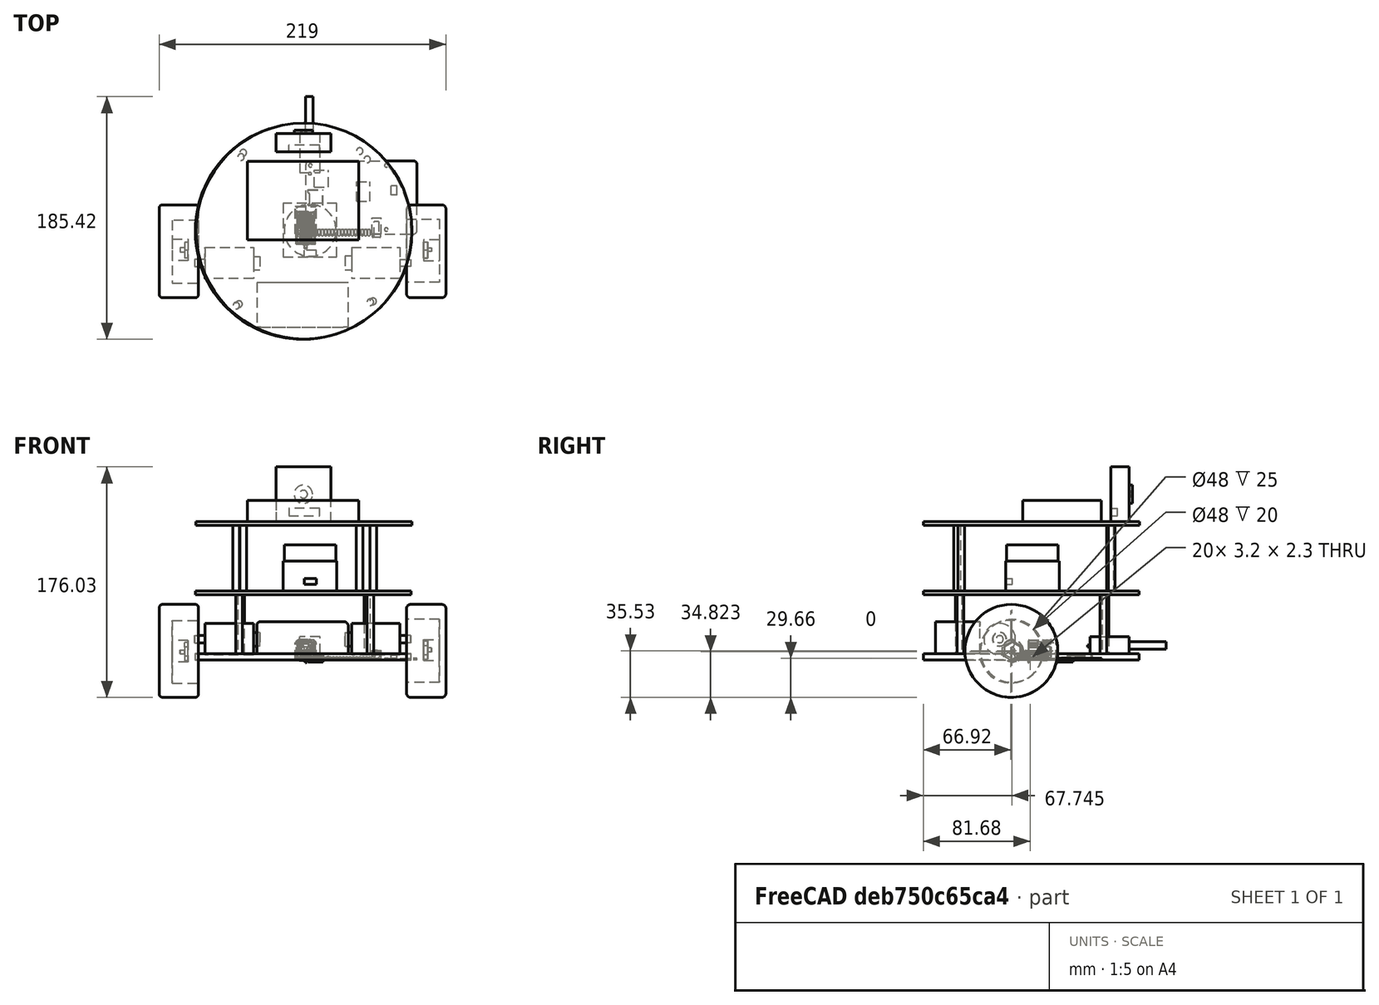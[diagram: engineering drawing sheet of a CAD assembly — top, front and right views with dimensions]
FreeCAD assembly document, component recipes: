
FREECAD ASSEMBLY — COMPONENT RECIPES ("futbot")

This assembly document has 9 components, labeled P0..P8 below (a component is one placed body or linked part). 8 of them carry a construction recipe — the FreeCAD feature program that regenerates the part from scratch, quoted from this document or its linked companion documents; the rest are supplied as boundary geometry only. No exploded tour is included for this assembly.
COMPONENT P0 — recipe-attached ("Cuerpo", modeled in this document).
Construction recipe (the document's own serialized feature program — sketch geometry with constraints, then the solid features built on it; lengths are millimeters unless a unit is written):

FEATURE [Sketcher::SketchObject] Sketch
  ArcFitTolerance = 1e-06
  AttachmentSupport = -> [XY_Plane]
  FullyConstrained = false
  MakeInternals = false
  MapMode = 5
  sketch-geometry (1):
    g0: Circle CenterX=-2.08618 CenterY=2.08626 CenterZ=0 NormalX=0 NormalY=0 NormalZ=1 AngleXU=0 Radius=82.5
  constraints (1):
    c: Diameter(g0) = 165
FEATURE [PartDesign::Pad] Pad
  Direction = (0,0,1)
  Length = 5
  Length2 = 10
  Profile = -> Sketch
  ReferenceAxis = -> Sketch [N_Axis]
  Refine = true
  Suppressed = false
  Type = 0
FEATURE [Sketcher::SketchObject] Sketch002
  ArcFitTolerance = 1e-06
  FullyConstrained = false
  MakeInternals = false
  MapMode = 5
  Placement = pos=(0,0,5) rot=(0,0,1;0rad)
  sketch-geometry (4):
    g0: LineSegment StartX=-37.4321 StartY=-37.1502 StartZ=0 EndX=-37.4321 EndY=-71.1502 EndZ=0
    g1: LineSegment StartX=-37.4321 StartY=-71.1502 StartZ=0 EndX=32.5679 EndY=-71.1502 EndZ=0
    g2: LineSegment StartX=32.5679 StartY=-71.1502 StartZ=0 EndX=32.5679 EndY=-37.1502 EndZ=0
    g3: LineSegment StartX=32.5679 StartY=-37.1502 StartZ=0 EndX=-37.4321 EndY=-37.1502 EndZ=0
  constraints (10):
    c: Coincident(g0,g1)
    c: Coincident(g1,g2)
    c: Coincident(g2,g3)
    c: Coincident(g3,g0)
    c: Vertical(g0)
    c: Vertical(g2)
    c: Horizontal(g1)
    c: Horizontal(g3)
    c: DistanceX(g3,g3) = 70
    c: DistanceY(g2,g2) = 34
FEATURE [PartDesign::Pad] Pad002
  BaseFeature = -> Pad
  Direction = (0,0,1)
  Length = 24.5
  Length2 = 10
  Profile = -> Sketch002
  ReferenceAxis = -> Sketch002 [N_Axis]
  Refine = true
  Suppressed = false
  Type = 0
FEATURE [Sketcher::SketchObject] Sketch003
  ArcFitTolerance = 1e-06
  AttachmentSupport = -> [Pad002]
  FullyConstrained = false
  MakeInternals = false
  MapMode = 5
  Placement = pos=(0,0,5) rot=(0,0,1;0rad)
  sketch-geometry (4):
    g0: Circle CenterX=-49.5124 CenterY=58.8774 CenterZ=0 NormalX=0 NormalY=0 NormalZ=1 AngleXU=0 Radius=2.5
    g1: Circle CenterX=46.9377 CenterY=57.0802 CenterZ=0 NormalX=0 NormalY=0 NormalZ=1 AngleXU=0 Radius=2.5
    g2: Circle CenterX=-51.0101 CenterY=-53.4481 CenterZ=0 NormalX=0 NormalY=0 NormalZ=1 AngleXU=0 Radius=2.5
    g3: Circle CenterX=49.334 CenterY=-51.9504 CenterZ=0 NormalX=0 NormalY=0 NormalZ=1 AngleXU=0 Radius=2.5
  constraints (4):
    c: Diameter(g0) = 5
    c: Diameter(g1) = 5
    c: Diameter(g2) = 5
    c: Diameter(g3) = 5
FEATURE [PartDesign::Pad] Pad003
  BaseFeature = -> Pad002
  Direction = (0,0,1)
  Length = 45
  Length2 = 10
  Profile = -> Sketch003
  ReferenceAxis = -> Sketch003 [N_Axis]
  Refine = true
  Suppressed = false
  Type = 0
FEATURE [PartDesign::Fillet] Fillet
  Base = -> Pad003 [Edge21]
  BaseFeature = -> Pad003
  Radius = 4
  Refine = true
  SupportTransform = false
  Suppressed = false
  UseAllEdges = false
FEATURE [PartDesign::Fillet] Fillet001
  Base = -> Fillet [Edge19]
  BaseFeature = -> Fillet
  Radius = 3
  Refine = true
  SupportTransform = false
  Suppressed = false
  UseAllEdges = false
FEATURE [PartDesign::Plane] DatumPlane
  AttachmentSupport = -> [Fillet001]
  Length = 198.362
  MapMode = 5
  Placement = pos=(0,0,50) rot=(0,0,1;0rad)
  ResizeMode = 0
  Width = 198.078
FEATURE [Sketcher::SketchObject] Sketch008
  ArcFitTolerance = 1e-06
  AttachmentSupport = -> [DatumPlane]
  FullyConstrained = false
  MakeInternals = false
  MapMode = 5
  Placement = pos=(0,0,50) rot=(0,0,1;0rad)
  sketch-geometry (1):
    g0: Circle CenterX=-1.91446 CenterY=2.09682 CenterZ=0 NormalX=0 NormalY=0 NormalZ=1 AngleXU=0 Radius=82.5
  constraints (1):
    c: Diameter(g0) = 165
FEATURE [PartDesign::Pad] Pad004
  BaseFeature = -> Fillet001
  Direction = (0,0,1)
  Length = 3
  Length2 = 10
  Profile = -> Sketch008
  ReferenceAxis = -> Sketch008 [N_Axis]
  Refine = true
  Suppressed = false
  Type = 0
FEATURE [Sketcher::SketchObject] Sketch024
  ArcFitTolerance = 1e-06
  FullyConstrained = false
  MakeInternals = false
  MapMode = 5
  Placement = pos=(0,79.2958,0) rot=(0,0.707107,0.707107;3.14159rad)
  sketch-geometry (4):
    g0: LineSegment StartX=-7.16249 StartY=80.5088 StartZ=0 EndX=-7.16249 EndY=65.5088 EndZ=0
    g1: LineSegment StartX=-7.16249 StartY=65.5088 StartZ=0 EndX=7.83751 EndY=65.5088 EndZ=0
    g2: LineSegment StartX=7.83751 StartY=65.5088 StartZ=0 EndX=7.83751 EndY=80.5088 EndZ=0
    g3: LineSegment StartX=7.83751 StartY=80.5088 StartZ=0 EndX=-7.16249 EndY=80.5088 EndZ=0
  constraints (10):
    c: Coincident(g0,g1)
    c: Coincident(g1,g2)
    c: Coincident(g2,g3)
    c: Coincident(g3,g0)
    c: Vertical(g0)
    c: Vertical(g2)
    c: Horizontal(g1)
    c: Horizontal(g3)
    c: DistanceX(g3,g3) = 15
    c: DistanceY(g2,g2) = 15
FEATURE [PartDesign::Pad] Pad006
  BaseFeature = -> Pad004
  Direction = (1e-16,1,-2e-16)
  Length = 10
  Length2 = 10
  Profile = -> Sketch024
  ReferenceAxis = -> Sketch024 [N_Axis]
  Refine = true
  Suppressed = false
  Type = 0
FEATURE [Sketcher::SketchObject] Sketch026
  ArcFitTolerance = 1e-06
  FullyConstrained = false
  MakeInternals = false
  MapMode = 5
  Placement = pos=(0,0,53) rot=(0,0,1;0rad)
  sketch-geometry (4):
    g0: Circle CenterX=-47.8055 CenterY=62.1638 CenterZ=0 NormalX=0 NormalY=0 NormalZ=1 AngleXU=0 Radius=2.5
    g1: Circle CenterX=41.1821 CenterY=63.4293 CenterZ=0 NormalX=0 NormalY=0 NormalZ=1 AngleXU=0 Radius=2.5
    g2: Circle CenterX=-53.1273 CenterY=-54.6618 CenterZ=0 NormalX=0 NormalY=0 NormalZ=1 AngleXU=0 Radius=2.5
    g3: Circle CenterX=51.4464 CenterY=-51.3399 CenterZ=0 NormalX=0 NormalY=0 NormalZ=1 AngleXU=0 Radius=2.5
  constraints (4):
    c: Diameter(g0) = 5
    c: Diameter(g1) = 5
    c: Diameter(g2) = 5
    c: Diameter(g3) = 5
FEATURE [PartDesign::Pad] Pad008
  BaseFeature = -> Pad006
  Direction = (0,0,1)
  Length = 50
  Length2 = 10
  Profile = -> Sketch026
  ReferenceAxis = -> Sketch026 [N_Axis]
  Refine = true
  Suppressed = false
  Type = 0
FEATURE [PartDesign::Plane] DatumPlane001
  AttachmentSupport = -> [Pad008]
  Length = 198.362
  MapMode = 5
  Placement = pos=(0,0,103) rot=(0,0,1;0rad)
  ResizeMode = 0
  Width = 198.078
FEATURE [Sketcher::SketchObject] Sketch027
  ArcFitTolerance = 1e-06
  AttachmentSupport = -> [DatumPlane001]
  FullyConstrained = false
  MakeInternals = false
  MapMode = 5
  Placement = pos=(0,0,103) rot=(0,0,1;0rad)
  sketch-geometry (1):
    g0: Circle CenterX=-1.38772 CenterY=2.31443 CenterZ=0 NormalX=0 NormalY=0 NormalZ=1 AngleXU=0 Radius=82.5
  constraints (1):
    c: Diameter(g0) = 165
FEATURE [PartDesign::Pad] Pad009
  BaseFeature = -> Pad008
  Direction = (0,0,1)
  Length = 3
  Length2 = 10
  Profile = -> Sketch027
  ReferenceAxis = -> Sketch027 [N_Axis]
  Refine = true
  Suppressed = false
  Type = 0
FEATURE [Sketcher::SketchObject] Sketch051
  ArcFitTolerance = 1e-06
  AttachmentSupport = -> [Pad009]
  FullyConstrained = false
  MakeInternals = false
  MapMode = 5
  Placement = pos=(0,0,106) rot=(0,0,1;0rad)
  sketch-geometry (4):
    g0: LineSegment StartX=-44.6333 StartY=55.601 StartZ=0 EndX=-44.6333 EndY=-4.39901 EndZ=0
    g1: LineSegment StartX=-44.6333 StartY=-4.39901 StartZ=0 EndX=40.3667 EndY=-4.39901 EndZ=0
    g2: LineSegment StartX=40.3667 StartY=-4.39901 StartZ=0 EndX=40.3667 EndY=55.601 EndZ=0
    g3: LineSegment StartX=40.3667 StartY=55.601 StartZ=0 EndX=-44.6333 EndY=55.601 EndZ=0
  constraints (10):
    c: Coincident(g0,g1)
    c: Coincident(g1,g2)
    c: Coincident(g2,g3)
    c: Coincident(g3,g0)
    c: Vertical(g0)
    c: Vertical(g2)
    c: Horizontal(g1)
    c: Horizontal(g3)
    c: DistanceX(g3,g3) = 85
    c: DistanceY(g0,g0) = 60
FEATURE [PartDesign::Pad] Pad025
  BaseFeature = -> Pad009
  Direction = (0,0,1)
  Length = 16
  Length2 = 10
  Profile = -> Sketch051
  ReferenceAxis = -> Sketch051 [N_Axis]
  Refine = true
  Suppressed = false
  Type = 0
FEATURE [PartDesign::Body] Body  label="Cuerpo"
  AllowCompound = false
  Group = -> [Sketch,Pad,Sketch002,Pad002,Sketch003,Pad003,Fillet,Fillet001,DatumPlane,Sketch008,Pad004,Sketch024,Pad006,Sketch026,Pad008,DatumPlane001,Sketch027,Pad009,Sketch051,Pad025]
  Origin = -> Origin
  Tip = -> Pad025
COMPONENT P1 — recipe-attached ("Body008", modeled in this document).
Construction recipe (the document's own serialized feature program — sketch geometry with constraints, then the solid features built on it; lengths are millimeters unless a unit is written):

FEATURE [Sketcher::SketchObject] Sketch030
  ArcFitTolerance = 1e-06
  AttachmentSupport = -> [YZ_Plane021]
  FullyConstrained = false
  MakeInternals = false
  MapMode = 5
  Placement = pos=(0,0,0) rot=(0.57735,0.57735,0.57735;2.0944rad)
  sketch-geometry (1):
    g0: Circle CenterX=-2.0864 CenterY=2.08625 CenterZ=0 NormalX=0 NormalY=0 NormalZ=1 AngleXU=0 Radius=35.5
  constraints (1):
    c: Diameter(g0) = 71
FEATURE [PartDesign::Pad] Pad012
  Direction = (1,0,0)
  Length = 30
  Length2 = 10
  Placement = pos=(0,0,0) rot=(1,1,1;2.0944rad)
  Profile = -> Sketch030
  ReferenceAxis = -> Sketch030 [N_Axis]
  Refine = true
  Suppressed = false
  Type = 0
FEATURE [Sketcher::SketchObject] Sketch031
  ArcFitTolerance = 1e-06
  AttachmentSupport = -> [Pad012]
  FullyConstrained = false
  MakeInternals = false
  MapMode = 5
  Placement = pos=(0,0,0) rot=(0.57735,0.57735,-0.57735;4.18879rad)
  sketch-geometry (1):
    g0: Circle CenterX=-1.66476 CenterY=-2.11974 CenterZ=0 NormalX=0 NormalY=0 NormalZ=1 AngleXU=0 Radius=24
  constraints (1):
    c: Diameter(g0) = 48
FEATURE [PartDesign::Pocket] Pocket
  BaseFeature = -> Pad012
  Direction = (1,0,0)
  Length = 25
  Length2 = 5
  Placement = pos=(0,0,0) rot=(1,1,1;2.0944rad)
  Profile = -> Sketch031
  ReferenceAxis = -> Sketch031 [N_Axis]
  Refine = true
  Suppressed = false
  Type = 0
FEATURE [Sketcher::SketchObject] Sketch032
  ArcFitTolerance = 1e-06
  AttachmentSupport = -> [Pocket]
  FullyConstrained = false
  MakeInternals = false
  MapMode = 5
  Placement = pos=(25,0,0) rot=(0.57735,0.57735,-0.57735;4.18879rad)
  sketch-geometry (1):
    g0: Circle CenterX=-1.35082 CenterY=-2.73267 CenterZ=0 NormalX=0 NormalY=0 NormalZ=1 AngleXU=0 Radius=8
  constraints (1):
    c: Diameter(g0) = 16
FEATURE [PartDesign::Pad] Pad013
  BaseFeature = -> Pocket
  Direction = (-1,0,0)
  Length = 12
  Length2 = 10
  Placement = pos=(0,0,0) rot=(1,1,1;2.0944rad)
  Profile = -> Sketch032
  ReferenceAxis = -> Sketch032 [N_Axis]
  Refine = true
  Suppressed = false
  Type = 0
FEATURE [Sketcher::SketchObject] Sketch033
  ArcFitTolerance = 1e-06
  AttachmentSupport = -> [Pad013]
  FullyConstrained = false
  MakeInternals = false
  MapMode = 5
  Placement = pos=(13,0,0) rot=(0.57735,0.57735,-0.57735;4.18879rad)
  sketch-geometry (7):
    g0: LineSegment StartX=-1.11187 StartY=4.24801 StartZ=0 EndX=-7.22276 EndY=0.700721 EndZ=0
    g1: LineSegment StartX=-7.22276 StartY=0.700721 StartZ=0 EndX=-7.20616 EndY=-6.36511 EndZ=0
    g2: LineSegment StartX=-7.20616 StartY=-6.36511 StartZ=0 EndX=-1.07867 EndY=-9.88365 EndZ=0
    g3: LineSegment StartX=-1.07867 StartY=-9.88365 StartZ=0 EndX=5.03222 EndY=-6.33636 EndZ=0
    g4: LineSegment StartX=5.03222 StartY=-6.33636 StartZ=0 EndX=5.01562 EndY=0.729474 EndZ=0
    g5: LineSegment StartX=5.01562 StartY=0.729474 StartZ=0 EndX=-1.11187 EndY=4.24801 EndZ=0
    g6: Circle [constr] CenterX=-1.09527 CenterY=-2.81782 CenterZ=0 NormalX=0 NormalY=0 NormalZ=1 AngleXU=0 Radius=7.06585
  constraints (13):
    c: Coincident(g0,g1)
    c: Coincident(g1,g2)
    c: Coincident(g2,g3)
    c: Coincident(g3,g4)
    c: Coincident(g4,g5)
    c: Coincident(g5,g0)
    c: Equal(g0, g1-g5) x5
    c: PointOnObject(g0,g6)
    c: PointOnObject(g1,g6)
    c: PointOnObject(g2,g6)
    c: PointOnObject(g3,g6)
    c: PointOnObject(g4,g6)
    c: PointOnObject(g5,g6)
FEATURE [PartDesign::Pocket] Pocket001
  BaseFeature = -> Pad013
  Direction = (1,0,0)
  Length = 3
  Length2 = 5
  Placement = pos=(0,0,0) rot=(1,1,1;2.0944rad)
  Profile = -> Sketch033
  ReferenceAxis = -> Sketch033 [N_Axis]
  Refine = true
  Suppressed = false
  Type = 0
FEATURE [Sketcher::SketchObject] Sketch004
  ArcFitTolerance = 1e-06
  AttachmentSupport = -> [Pocket001]
  FullyConstrained = false
  MakeInternals = false
  MapMode = 5
  Placement = pos=(16,0,0) rot=(0.57735,0.57735,-0.57735;4.18879rad)
  sketch-geometry (1):
    g0: Circle CenterX=-0.927213 CenterY=-2.79304 CenterZ=0 NormalX=0 NormalY=0 NormalZ=1 AngleXU=0 Radius=1.5
  constraints (1):
    c: Diameter(g0) = 3
FEATURE [PartDesign::Pocket] Pocket002
  BaseFeature = -> Pocket001
  Direction = (1,0,0)
  Length = 3
  Length2 = 5
  Placement = pos=(0,0,0) rot=(1,1,1;2.0944rad)
  Profile = -> Sketch004
  ReferenceAxis = -> Sketch004 [N_Axis]
  Refine = true
  Suppressed = false
  Type = 0
FEATURE [PartDesign::Fillet] Fillet016  label="Fillet018"
  Base = -> Pocket002 [Edge2]
  BaseFeature = -> Pocket002
  Placement = pos=(0,0,0) rot=(1,1,1;2.0944rad)
  Radius = 3
  Refine = true
  SupportTransform = false
  Suppressed = false
  UseAllEdges = false
FEATURE [PartDesign::Fillet] Fillet017  label="Fillet019"
  Base = -> Fillet016 [Edge3]
  BaseFeature = -> Fillet016
  Placement = pos=(0,0,0) rot=(1,1,1;2.0944rad)
  Radius = 3
  Refine = true
  SupportTransform = false
  Suppressed = false
  UseAllEdges = false
FEATURE [PartDesign::Body] Body001  label="Body008"
  AllowCompound = false
  Group = -> [Sketch030,Pad012,Sketch031,Pocket,Sketch032,Pad013,Sketch033,Pocket001,Sketch004,Pocket002,Fillet016,Fillet017]
  Origin = -> Origin021
  Placement = pos=(77,-11,5) rot=(0,0,1;0rad)
  Tip = -> Fillet017
COMPONENT P2 — recipe-attached ("Body009", modeled in this document).
Construction recipe (the document's own serialized feature program — sketch geometry with constraints, then the solid features built on it; lengths are millimeters unless a unit is written):

FEATURE [Sketcher::SketchObject] Sketch034
  ArcFitTolerance = 1e-06
  AttachmentSupport = -> [YZ_Plane022]
  FullyConstrained = false
  MakeInternals = false
  MapMode = 5
  Placement = pos=(0,0,0) rot=(0.57735,0.57735,0.57735;2.0944rad)
  sketch-geometry (1):
    g0: Circle CenterX=-2.08628 CenterY=2.08615 CenterZ=0 NormalX=0 NormalY=0 NormalZ=1 AngleXU=0 Radius=35.5
  constraints (1):
    c: Diameter(g0) = 71
FEATURE [PartDesign::Pad] Pad014
  Direction = (1,0,0)
  Length = 30
  Length2 = 10
  Placement = pos=(0,0,0) rot=(1,1,1;2.0944rad)
  Profile = -> Sketch034
  ReferenceAxis = -> Sketch034 [N_Axis]
  Refine = true
  Suppressed = false
  Type = 0
FEATURE [Sketcher::SketchObject] Sketch035
  ArcFitTolerance = 1e-06
  AttachmentSupport = -> [Pad014]
  FullyConstrained = false
  MakeInternals = false
  MapMode = 5
  Placement = pos=(30,0,0) rot=(0.57735,0.57735,0.57735;2.0944rad)
  sketch-geometry (1):
    g0: Circle CenterX=-2.49007 CenterY=1.41343 CenterZ=0 NormalX=0 NormalY=0 NormalZ=1 AngleXU=0 Radius=24
  constraints (1):
    c: Diameter(g0) = 48
FEATURE [PartDesign::Fillet] Fillet018  label="Fillet020"
  Base = -> Pad014 [Edge3]
  BaseFeature = -> Pad014
  Placement = pos=(0,0,0) rot=(1,1,1;2.0944rad)
  Radius = 2.5
  Refine = true
  SupportTransform = false
  Suppressed = false
  UseAllEdges = false
FEATURE [PartDesign::Fillet] Fillet019  label="Fillet021"
  Base = -> Fillet018 [Edge3]
  BaseFeature = -> Fillet018
  Placement = pos=(0,0,0) rot=(1,1,1;2.0944rad)
  Radius = 2.5
  Refine = true
  SupportTransform = false
  Suppressed = false
  UseAllEdges = false
FEATURE [PartDesign::Pocket] Pocket003
  BaseFeature = -> Fillet019
  Direction = (-1,0,0)
  Length = 20
  Length2 = 5
  Placement = pos=(0,0,0) rot=(1,1,1;2.0944rad)
  Profile = -> Sketch035
  ReferenceAxis = -> Sketch035 [N_Axis]
  Refine = true
  Suppressed = false
  Type = 0
FEATURE [Sketcher::SketchObject] Sketch036
  ArcFitTolerance = 1e-06
  AttachmentSupport = -> [Pocket003]
  FullyConstrained = false
  MakeInternals = false
  MapMode = 5
  Placement = pos=(10,0,0) rot=(0.57735,0.57735,0.57735;2.0944rad)
  sketch-geometry (1):
    g0: Circle CenterX=-1.10678 CenterY=1.90225 CenterZ=0 NormalX=0 NormalY=0 NormalZ=1 AngleXU=0 Radius=8.25
  constraints (1):
    c: Diameter(g0) = 16.5
FEATURE [PartDesign::Pad] Pad015
  BaseFeature = -> Pocket003
  Direction = (1,0,0)
  Length = 12
  Length2 = 10
  Placement = pos=(0,0,0) rot=(1,1,1;2.0944rad)
  Profile = -> Sketch036
  ReferenceAxis = -> Sketch036 [N_Axis]
  Refine = true
  Suppressed = false
  Type = 0
FEATURE [Sketcher::SketchObject] Sketch037
  ArcFitTolerance = 1e-06
  AttachmentSupport = -> [Pad015]
  FullyConstrained = false
  MakeInternals = false
  MapMode = 5
  Placement = pos=(22,0,0) rot=(0.57735,0.57735,0.57735;2.0944rad)
  sketch-geometry (7):
    g0: LineSegment StartX=4.85295 StartY=4.98885 StartZ=0 EndX=-1.20923 EndY=8.48885 EndZ=0
    g1: LineSegment StartX=-1.20923 StartY=8.48885 StartZ=0 EndX=-7.27141 EndY=4.98885 EndZ=0
    g2: LineSegment StartX=-7.27141 StartY=4.98885 StartZ=0 EndX=-7.27141 EndY=-2.01115 EndZ=0
    g3: LineSegment StartX=-7.27141 StartY=-2.01115 StartZ=0 EndX=-1.20923 EndY=-5.51115 EndZ=0
    g4: LineSegment StartX=-1.20923 StartY=-5.51115 StartZ=0 EndX=4.85295 EndY=-2.01115 EndZ=0
    g5: LineSegment StartX=4.85295 StartY=-2.01115 StartZ=0 EndX=4.85295 EndY=4.98885 EndZ=0
    g6: Circle [constr] CenterX=-1.20923 CenterY=1.48885 CenterZ=0 NormalX=0 NormalY=0 NormalZ=1 AngleXU=0 Radius=7
  constraints (15):
    c: Coincident(g0,g1)
    c: Coincident(g1,g2)
    c: Coincident(g2,g3)
    c: Coincident(g3,g4)
    c: Coincident(g4,g5)
    c: Coincident(g5,g0)
    c: Equal(g0, g1-g5) x5
    c: PointOnObject(g0,g6)
    c: PointOnObject(g1,g6)
    c: PointOnObject(g2,g6)
    c: PointOnObject(g3,g6)
    c: PointOnObject(g4,g6)
    c: PointOnObject(g5,g6)
    c: Distance(g0,g0) = 7
    c: DistanceY(g5,g5) = 7
FEATURE [PartDesign::Pocket] Pocket004
  BaseFeature = -> Pad015
  Direction = (-1,0,0)
  Length = 2.5
  Length2 = 5
  Placement = pos=(0,0,0) rot=(1,1,1;2.0944rad)
  Profile = -> Sketch037
  ReferenceAxis = -> Sketch037 [N_Axis]
  Refine = true
  Suppressed = false
  Type = 0
FEATURE [Sketcher::SketchObject] Sketch038
  ArcFitTolerance = 1e-06
  AttachmentSupport = -> [Pocket004]
  FullyConstrained = false
  MakeInternals = false
  MapMode = 5
  Placement = pos=(19.5,0,0) rot=(0.57735,0.57735,0.57735;2.0944rad)
  sketch-geometry (1):
    g0: Circle CenterX=-1.04009 CenterY=1.34355 CenterZ=0 NormalX=0 NormalY=0 NormalZ=1 AngleXU=0 Radius=1.5
  constraints (1):
    c: Diameter(g0) = 3
FEATURE [PartDesign::Pocket] Pocket005
  BaseFeature = -> Pocket004
  Direction = (-1,0,0)
  Length = 3.5
  Length2 = 5
  Placement = pos=(0,0,0) rot=(1,1,1;2.0944rad)
  Profile = -> Sketch038
  ReferenceAxis = -> Sketch038 [N_Axis]
  Refine = true
  Suppressed = false
  Type = 0
FEATURE [PartDesign::Body] Body002  label="Body009"
  AllowCompound = false
  Group = -> [Sketch034,Pad014,Sketch035,Fillet018,Fillet019,Pocket003,Sketch036,Pad015,Sketch037,Pocket004,Sketch038,Pocket005]
  Origin = -> Origin022
  Placement = pos=(-112,-11,5) rot=(0,0,1;0rad)
  Tip = -> Pocket005
COMPONENT P3 — recipe-attached ("Body010", modeled in this document).
Construction recipe (the document's own serialized feature program — sketch geometry with constraints, then the solid features built on it; lengths are millimeters unless a unit is written):

FEATURE [Sketcher::SketchObject] Sketch039
  ArcFitTolerance = 1e-06
  AttachmentSupport = -> [XY_Plane023]
  FullyConstrained = false
  MakeInternals = false
  MapMode = 5
  sketch-geometry (4):
    g0: LineSegment StartX=-17.3005 StartY=23.5417 StartZ=0 EndX=-17.3005 EndY=-17.4583 EndZ=0
    g1: LineSegment StartX=-17.3005 StartY=-17.4583 StartZ=0 EndX=23.6995 EndY=-17.4583 EndZ=0
    g2: LineSegment StartX=23.6995 StartY=-17.4583 StartZ=0 EndX=23.6995 EndY=23.5417 EndZ=0
    g3: LineSegment StartX=23.6995 StartY=23.5417 StartZ=0 EndX=-17.3005 EndY=23.5417 EndZ=0
  constraints (10):
    c: Coincident(g0,g1)
    c: Coincident(g1,g2)
    c: Coincident(g2,g3)
    c: Coincident(g3,g0)
    c: Vertical(g0)
    c: Vertical(g2)
    c: Horizontal(g1)
    c: Horizontal(g3)
    c: DistanceX(g1,g1) = 41
    c: DistanceY(g0,g0) = 41
FEATURE [PartDesign::Pad] Pad016
  Direction = (0,0,1)
  Length = 22.6
  Length2 = 10
  Profile = -> Sketch039
  ReferenceAxis = -> Sketch039 [N_Axis]
  Refine = true
  Suppressed = false
  Type = 0
FEATURE [Sketcher::SketchObject] Sketch040
  ArcFitTolerance = 1e-06
  AttachmentSupport = -> [Pad016]
  FullyConstrained = false
  MakeInternals = false
  MapMode = 5
  Placement = pos=(0,0,22.6) rot=(0,0,1;0rad)
  sketch-geometry (1):
    g0: Circle CenterX=3.29703 CenterY=2.8924 CenterZ=0 NormalX=0 NormalY=0 NormalZ=1 AngleXU=0 Radius=19.8
  constraints (1):
    c: Diameter(g0) = 39.6
FEATURE [PartDesign::Pad] Pad017
  BaseFeature = -> Pad016
  Direction = (0,0,1)
  Length = 12.6
  Length2 = 10
  Profile = -> Sketch040
  ReferenceAxis = -> Sketch040 [N_Axis]
  Refine = true
  Suppressed = false
  Type = 0
FEATURE [Sketcher::SketchObject] Sketch041
  ArcFitTolerance = 1e-06
  AttachmentSupport = -> [Pad017]
  FullyConstrained = false
  MakeInternals = false
  MapMode = 5
  Placement = pos=(0,-17.4583,0) rot=(1,0,0;1.5708rad)
  sketch-geometry (5):
    g0: LineSegment StartX=-1.04287 StartY=9.49271 StartZ=0 EndX=-1.04287 EndY=4.79271 EndZ=0
    g1: LineSegment StartX=-1.04287 StartY=4.79271 StartZ=0 EndX=7.95713 EndY=4.79271 EndZ=0
    g2: LineSegment StartX=7.95713 StartY=4.79271 StartZ=0 EndX=7.95713 EndY=9.49271 EndZ=0
    g3: LineSegment StartX=7.95713 StartY=9.49271 StartZ=0 EndX=-1.04287 EndY=9.49271 EndZ=0
    g4: GeomPoint [constr] X=3.45713 Y=7.14271 Z=0
  constraints (11):
    c: Coincident(g0,g1)
    c: Coincident(g1,g2)
    c: Coincident(g2,g3)
    c: Coincident(g3,g0)
    c: Vertical(g0)
    c: Vertical(g2)
    c: Horizontal(g1)
    c: Horizontal(g3)
    c: Symmetric(g2,g0,g4)
    c: DistanceX(g3,g3) = 9
    c: DistanceY(g2,g2) = 4.7
FEATURE [PartDesign::Pocket] Pocket006
  BaseFeature = -> Pad017
  Direction = (0,1,-2e-16)
  Length = 5
  Length2 = 5
  Profile = -> Sketch041
  ReferenceAxis = -> Sketch041 [N_Axis]
  Refine = true
  Suppressed = false
  Type = 0
FEATURE [PartDesign::Body] Body003  label="Body010"
  AllowCompound = false
  Group = -> [Sketch039,Pad016,Sketch040,Pad017,Sketch041,Pocket006]
  Origin = -> Origin023
  Placement = pos=(0,0,53) rot=(0,0,1;0rad)
  Tip = -> Pocket006
COMPONENT P4 — recipe-attached ("Body011", modeled in this document).
Construction recipe (the document's own serialized feature program — sketch geometry with constraints, then the solid features built on it; lengths are millimeters unless a unit is written):

FEATURE [Sketcher::SketchObject] Sketch042
  ArcFitTolerance = 1e-06
  AttachmentSupport = -> [YZ_Plane024]
  FullyConstrained = true
  MakeInternals = false
  MapMode = 5
  Placement = pos=(0,0,0) rot=(0.57735,0.57735,0.57735;2.0944rad)
  sketch-geometry (1):
    g0: Circle CenterX=0 CenterY=0 CenterZ=0 NormalX=0 NormalY=0 NormalZ=1 AngleXU=0 Radius=12
  constraints (2):
    c: Coincident(g0,g-1)
    c: Diameter(g0) = 24
FEATURE [PartDesign::Pad] Pad018
  Direction = (1,0,0)
  Length = 37
  Length2 = 10
  Placement = pos=(0,0,0) rot=(1,1,1;2.0944rad)
  Profile = -> Sketch042
  ReferenceAxis = -> Sketch042 [N_Axis]
  Refine = true
  Suppressed = false
  Type = 0
FEATURE [Sketcher::SketchObject] Sketch001
  ArcFitTolerance = 1e-06
  AttachmentSupport = -> [Pad018]
  FullyConstrained = false
  MakeInternals = false
  MapMode = 5
  Placement = pos=(37,0,0) rot=(0.57735,0.57735,0.57735;2.0944rad)
  sketch-geometry (1):
    g0: Circle CenterX=-0.336656 CenterY=0 CenterZ=0 NormalX=0 NormalY=0 NormalZ=1 AngleXU=0 Radius=5.25
  constraints (2):
    c: PointOnObject(g0,g-1)
    c: Diameter(g0) = 10.5
FEATURE [PartDesign::Pad] Pad001
  BaseFeature = -> Pad018
  Direction = (1,0,0)
  Length = 5
  Length2 = 10
  Placement = pos=(0,0,0) rot=(1,1,1;2.0944rad)
  Profile = -> Sketch001
  ReferenceAxis = -> Sketch001 [N_Axis]
  Refine = true
  Suppressed = false
  Type = 0
FEATURE [Sketcher::SketchObject] Sketch043
  ArcFitTolerance = 1e-06
  AttachmentSupport = -> [Pad001]
  FullyConstrained = true
  MakeInternals = false
  MapMode = 5
  Placement = pos=(0,0,0) rot=(0.57735,0.57735,-0.57735;4.18879rad)
  sketch-geometry (1):
    g0: Circle CenterX=0 CenterY=0 CenterZ=0 NormalX=0 NormalY=0 NormalZ=1 AngleXU=0 Radius=2.75
  constraints (2):
    c: Coincident(g0,g-1)
    c: Diameter(g0) = 5.5
FEATURE [PartDesign::Pad] Pad019
  BaseFeature = -> Pad001
  Direction = (-1,0,0)
  Length = 8
  Length2 = 10
  Placement = pos=(0,0,0) rot=(1,1,1;2.0944rad)
  Profile = -> Sketch043
  ReferenceAxis = -> Sketch043 [N_Axis]
  Refine = true
  Suppressed = false
  Type = 0
  UseCustomVector = true
FEATURE [PartDesign::Body] Body004  label="Body011"
  AllowCompound = false
  Group = -> [Sketch042,Pad018,Sketch001,Pad001,Sketch043,Pad019]
  Origin = -> Origin024
  Placement = pos=(-77,-22,16) rot=(0,0,1;0rad)
  Tip = -> Pad019
COMPONENT P5 — recipe-attached ("Body012", modeled in this document).
Construction recipe (the document's own serialized feature program — sketch geometry with constraints, then the solid features built on it; lengths are millimeters unless a unit is written):

FEATURE [Sketcher::SketchObject] Sketch044
  ArcFitTolerance = 1e-06
  AttachmentSupport = -> [YZ_Plane025]
  FullyConstrained = true
  MakeInternals = false
  MapMode = 5
  Placement = pos=(0,0,0) rot=(0.57735,0.57735,0.57735;2.0944rad)
  sketch-geometry (1):
    g0: Circle CenterX=0 CenterY=0 CenterZ=0 NormalX=0 NormalY=0 NormalZ=1 AngleXU=0 Radius=12
  constraints (2):
    c: Coincident(g0,g-1)
    c: Diameter(g0) = 24
FEATURE [PartDesign::Pad] Pad020
  Direction = (1,0,0)
  Length = 37
  Length2 = 10
  Placement = pos=(0,0,0) rot=(1,1,1;2.0944rad)
  Profile = -> Sketch044
  ReferenceAxis = -> Sketch044 [N_Axis]
  Refine = true
  Suppressed = false
  Type = 0
FEATURE [Sketcher::SketchObject] Sketch045
  ArcFitTolerance = 1e-06
  AttachmentSupport = -> [Pad020]
  FullyConstrained = true
  MakeInternals = false
  MapMode = 5
  Placement = pos=(37,0,0) rot=(0.57735,0.57735,0.57735;2.0944rad)
  sketch-geometry (1):
    g0: Circle CenterX=0 CenterY=0 CenterZ=0 NormalX=0 NormalY=0 NormalZ=1 AngleXU=0 Radius=2.75
  constraints (2):
    c: Coincident(g0,g-1)
    c: Diameter(g0) = 5.5
FEATURE [PartDesign::Pad] Pad021
  BaseFeature = -> Pad020
  Direction = (1,0,0)
  Length = 8
  Length2 = 10
  Placement = pos=(0,0,0) rot=(1,1,1;2.0944rad)
  Profile = -> Sketch045
  ReferenceAxis = -> Sketch045 [N_Axis]
  Refine = true
  Suppressed = false
  Type = 0
FEATURE [Sketcher::SketchObject] Sketch046
  ArcFitTolerance = 1e-06
  AttachmentSupport = -> [Pad021]
  FullyConstrained = true
  MakeInternals = false
  MapMode = 5
  Placement = pos=(0,0,0) rot=(0.57735,0.57735,-0.57735;4.18879rad)
  sketch-geometry (1):
    g0: Circle CenterX=0 CenterY=0 CenterZ=0 NormalX=0 NormalY=0 NormalZ=1 AngleXU=0 Radius=5.25
  constraints (2):
    c: Coincident(g0,g-1)
    c: Diameter(g0) = 10.5
FEATURE [PartDesign::Pad] Pad022
  BaseFeature = -> Pad021
  Direction = (-1,0,0)
  Length = 5
  Length2 = 10
  Placement = pos=(0,0,0) rot=(1,1,1;2.0944rad)
  Profile = -> Sketch046
  ReferenceAxis = -> Sketch046 [N_Axis]
  Refine = true
  Suppressed = false
  Type = 0
FEATURE [PartDesign::Body] Body005  label="Body012"
  AllowCompound = false
  Group = -> [Sketch044,Pad020,Sketch045,Pad021,Sketch046,Pad022]
  Origin = -> Origin025
  Placement = pos=(35,-22,16) rot=(0,0,1;0rad)
  Tip = -> Pad022
COMPONENT P6 — recipe-attached ("Body013", modeled in this document).
Construction recipe (the document's own serialized feature program — sketch geometry with constraints, then the solid features built on it; lengths are millimeters unless a unit is written):

FEATURE [Sketcher::SketchObject] Sketch047
  ArcFitTolerance = 1e-06
  AttachmentSupport = -> [XZ_Plane026]
  FullyConstrained = false
  MakeInternals = false
  MapMode = 5
  Placement = pos=(0,0,0) rot=(1,0,0;1.5708rad)
  sketch-geometry (4):
    g0: LineSegment StartX=-12.8525 StartY=11.6213 StartZ=0 EndX=-12.8525 EndY=-30.3787 EndZ=0
    g1: LineSegment StartX=-12.8525 StartY=-30.3787 StartZ=0 EndX=29.1475 EndY=-30.3787 EndZ=0
    g2: LineSegment StartX=29.1475 StartY=-30.3787 StartZ=0 EndX=29.1475 EndY=11.6213 EndZ=0
    g3: LineSegment StartX=29.1475 StartY=11.6213 StartZ=0 EndX=-12.8525 EndY=11.6213 EndZ=0
  constraints (10):
    c: Coincident(g0,g1)
    c: Coincident(g1,g2)
    c: Coincident(g2,g3)
    c: Coincident(g3,g0)
    c: Vertical(g0)
    c: Vertical(g2)
    c: Horizontal(g1)
    c: Horizontal(g3)
    c: DistanceX(g3,g3) = 42
    c: DistanceY(g0,g0) = 42
FEATURE [PartDesign::Pad] Pad023
  Direction = (0,-1,2e-16)
  Length = 14
  Length2 = 10
  Placement = pos=(0,0,0) rot=(1,0,0;1.5708rad)
  Profile = -> Sketch047
  ReferenceAxis = -> Sketch047 [N_Axis]
  Refine = true
  Suppressed = false
  Type = 0
FEATURE [Sketcher::SketchObject] Sketch048
  ArcFitTolerance = 1e-06
  AttachmentSupport = -> [Pad023]
  FullyConstrained = false
  MakeInternals = false
  MapMode = 5
  Placement = pos=(0,-2.1e-15,0) rot=(-1,0,0;1.5708rad)
  sketch-geometry (1):
    g0: Circle CenterX=8.14286 CenterY=9.21914 CenterZ=0 NormalX=0 NormalY=0 NormalZ=1 AngleXU=0 Radius=7
  constraints (1):
    c: Diameter(g0) = 14
FEATURE [PartDesign::Pad] Pad024
  BaseFeature = -> Pad023
  Direction = (0,1,2e-16)
  Length = 2.5
  Length2 = 10
  Placement = pos=(0,0,0) rot=(1,0,0;1.5708rad)
  Profile = -> Sketch048
  ReferenceAxis = -> Sketch048 [N_Axis]
  Refine = true
  Suppressed = false
  Type = 0
FEATURE [Sketcher::SketchObject] Sketch049
  ArcFitTolerance = 1e-06
  AttachmentSupport = -> [Pad024]
  FullyConstrained = false
  MakeInternals = false
  MapMode = 5
  Placement = pos=(0,2.5,0) rot=(-1,0,0;1.5708rad)
  sketch-geometry (1):
    g0: Circle CenterX=8.27745 CenterY=9.21909 CenterZ=0 NormalX=0 NormalY=0 NormalZ=1 AngleXU=0 Radius=5.62223
FEATURE [PartDesign::Hole] Hole
  BaseFeature = -> Pad024
  CustomThreadClearance = 0
  Depth = 0.5
  DepthType = 0
  Diameter = 6
  DrillForDepth = false
  DrillPoint = 1
  DrillPointAngle = 118
  HoleCutCountersinkAngle = 90
  HoleCutCustomValues = false
  HoleCutDepth = 0
  HoleCutDiameter = 6.1
  HoleCutType = 0
  ModelThread = false
  Placement = pos=(0,0,0) rot=(1,0,0;1.5708rad)
  Profile = -> Sketch049
  Refine = true
  Suppressed = false
  Tapered = false
  TaperedAngle = 90
  ThreadClass = 0
  ThreadDepth = 0.5
  ThreadDepthType = 0
  ThreadDirection = 0
  ThreadFit = 0
  ThreadSize = 0
  ThreadType = 0
  Threaded = false
  UseCustomThreadClearance = false
FEATURE [Sketcher::SketchObject] Sketch050
  ArcFitTolerance = 1e-06
  AttachmentSupport = -> [Hole]
  FullyConstrained = false
  MakeInternals = false
  MapMode = 5
  Placement = pos=(0,-14,0) rot=(1,0,0;1.5708rad)
  sketch-geometry (4):
    g0: LineSegment StartX=-3.02818 StartY=-20.0516 StartZ=0 EndX=-3.02818 EndY=-25.5516 EndZ=0
    g1: LineSegment StartX=-3.02818 StartY=-25.5516 StartZ=0 EndX=20.4718 EndY=-25.5516 EndZ=0
    g2: LineSegment StartX=20.4718 StartY=-25.5516 StartZ=0 EndX=20.4718 EndY=-20.0516 EndZ=0
    g3: LineSegment StartX=20.4718 StartY=-20.0516 StartZ=0 EndX=-3.02818 EndY=-20.0516 EndZ=0
  constraints (10):
    c: Coincident(g0,g1)
    c: Coincident(g1,g2)
    c: Coincident(g2,g3)
    c: Coincident(g3,g0)
    c: Vertical(g0)
    c: Vertical(g2)
    c: Horizontal(g1)
    c: Horizontal(g3)
    c: DistanceX(g3,g3) = 23.5
    c: DistanceY(g0,g0) = 5.5
FEATURE [PartDesign::Pocket] Pocket007
  BaseFeature = -> Hole
  Direction = (0,1,-2e-16)
  Length = 5
  Length2 = 5
  Placement = pos=(0,0,0) rot=(1,0,0;1.5708rad)
  Profile = -> Sketch050
  ReferenceAxis = -> Sketch050 [N_Axis]
  Refine = true
  Suppressed = false
  Type = 0
FEATURE [PartDesign::Body] Body006  label="Body013"
  AllowCompound = false
  Group = -> [Sketch047,Pad023,Sketch048,Pad024,Sketch049,Hole,Sketch050,Pocket007]
  Origin = -> Origin026
  Placement = pos=(-10,77,136) rot=(0,0,1;0rad)
  Tip = -> Pocket007
COMPONENT P7 — recipe-attached ("Body014", modeled in this document).
Construction recipe (the document's own serialized feature program — sketch geometry with constraints, then the solid features built on it; lengths are millimeters unless a unit is written):

FEATURE [Sketcher::SketchObject] Sketch052
  ArcFitTolerance = 1e-06
  AttachmentSupport = -> [XY_Plane027]
  FullyConstrained = false
  MakeInternals = false
  MapMode = 5
  sketch-geometry (4):
    g0: LineSegment StartX=-4.70785 StartY=9.00794 StartZ=0 EndX=-4.70785 EndY=-20.9921 EndZ=0
    g1: LineSegment StartX=-4.70785 StartY=-20.9921 StartZ=0 EndX=10.8922 EndY=-20.9921 EndZ=0
    g2: LineSegment StartX=10.8922 StartY=-20.9921 StartZ=0 EndX=10.8922 EndY=9.00794 EndZ=0
    g3: LineSegment StartX=10.8922 StartY=9.00794 StartZ=0 EndX=-4.70785 EndY=9.00794 EndZ=0
  constraints (10):
    c: Coincident(g0,g1)
    c: Coincident(g1,g2)
    c: Coincident(g2,g3)
    c: Coincident(g3,g0)
    c: Vertical(g0)
    c: Vertical(g2)
    c: Horizontal(g1)
    c: Horizontal(g3)
    c: DistanceX(g1,g1) = 15.6
    c: DistanceY(g2,g2) = 30
FEATURE [PartDesign::Pad] Pad026
  Direction = (0,0,1)
  Length = 13
  Length2 = 10
  Profile = -> Sketch052
  ReferenceAxis = -> Sketch052 [N_Axis]
  Refine = true
  Suppressed = false
  Type = 0
FEATURE [Sketcher::SketchObject] Sketch053
  ArcFitTolerance = 1e-06
  AttachmentSupport = -> [Pad026]
  FullyConstrained = false
  MakeInternals = false
  MapMode = 5
  Placement = pos=(0,9.00794,0) rot=(0,0.707107,0.707107;3.14159rad)
  sketch-geometry (1):
    g0: Circle CenterX=-2.70878 CenterY=6.23385 CenterZ=0 NormalX=0 NormalY=0 NormalZ=1 AngleXU=0 Radius=2.85
  constraints (1):
    c: Diameter(g0) = 5.7
FEATURE [PartDesign::Pad] Pad027
  BaseFeature = -> Pad026
  Direction = (0,1,-2e-16)
  Length = 28
  Length2 = 10
  Profile = -> Sketch053
  ReferenceAxis = -> Sketch053 [N_Axis]
  Refine = true
  Suppressed = false
  Type = 0
FEATURE [Sketcher::SketchObject] Sketch054
  ArcFitTolerance = 1e-06
  AttachmentSupport = -> [Pad027]
  FullyConstrained = false
  MakeInternals = false
  MapMode = 5
  Placement = pos=(0,-20.9921,0) rot=(1,0,0;1.5708rad)
  sketch-geometry (1):
    g0: Circle CenterX=3.02825 CenterY=5.85558 CenterZ=0 NormalX=0 NormalY=0 NormalZ=1 AngleXU=0 Radius=0.75
  constraints (1):
    c: Diameter(g0) = 1.5
FEATURE [PartDesign::Pad] Pad028
  BaseFeature = -> Pad027
  Direction = (0,-1,2e-16)
  Length = 2
  Length2 = 10
  Profile = -> Sketch054
  ReferenceAxis = -> Sketch054 [N_Axis]
  Refine = true
  Suppressed = false
  Type = 0
FEATURE [PartDesign::Body] Body007  label="Body014"
  AllowCompound = false
  Group = -> [Sketch052,Pad026,Sketch053,Pad027,Sketch054,Pad028]
  Origin = -> Origin027
  Placement = pos=(0,68,5) rot=(0,0,1;0rad)
  Tip = -> Pad028
COMPONENT P8 — geometry summary ("PCBA: Raspberry Pi 4B"; no construction recipe available for this part):
  bounding box: 90.1 x 58.5 x 19.0 mm
  tessellated surface: 24,702 triangles
  volume: 18599 mm^3 (19% of its bounding box)
PROVENANCE & LICENSES
A FreeCAD (.FCStd) document from a public repository crawl; recipes are the document's own serialized feature recipes (and, for linked parts, companion documents' recipes).
License: mit.
